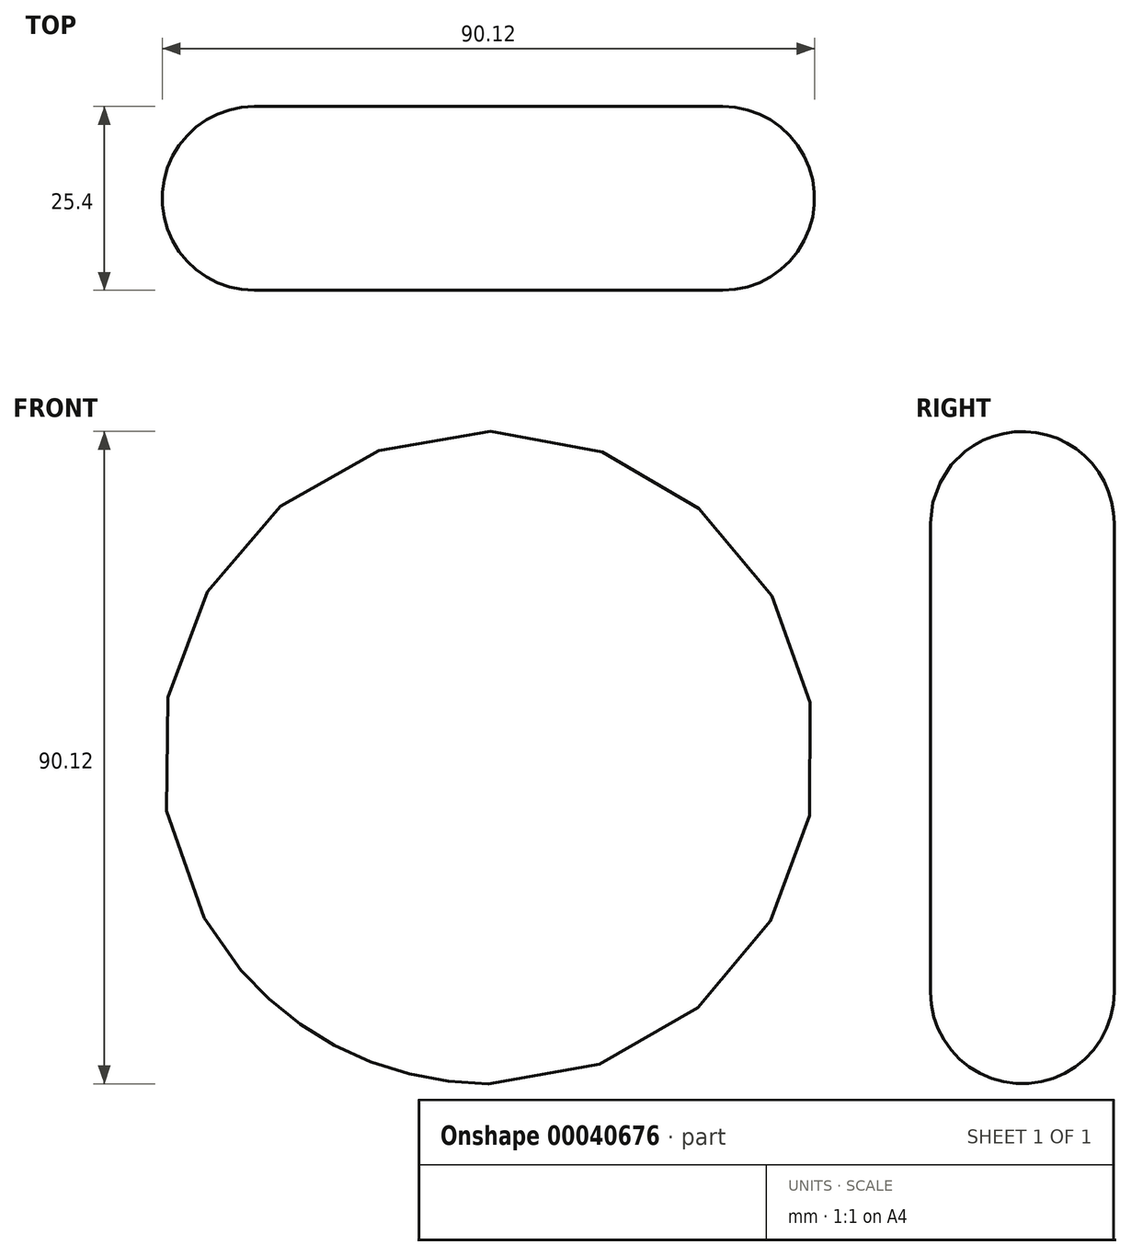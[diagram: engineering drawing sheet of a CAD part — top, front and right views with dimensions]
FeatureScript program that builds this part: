
annotation { "Feature Type Name" : "Feature", "Feature Type Description" : "" }
export const myFeature = defineFeature(function(context is Context, id is Id, definition is map)
    precondition{}
    {
        {
            var Q0;
            Q0=qCreatedBy(makeId("Front.planeOp"),FACE);
            var sketch = newSketch(context, id + "F0", { "sketchPlane" : qUnion([Q0])});
            skCircle(sketch, "E0", {"center": v(0, 0) * mm, "radius": 45.06 * mm});
            skSolve(sketch);
        }
        {
            var Q0;
            Q0 = qSketchRegion(id + "F0", true);
            var Q1;
            Q1=makeQuery(id+"F0.imprint","IMPRINT",FACE,{"disambiguationData":[TD([[makeQuery(id+"F0.imprint","IMPRINT",EDGE,{"derivedFrom":sQuery(id+"F0.wireOp",EDGE,"E0")}),1.0]])]});
            extrude(context, id + "F1", {"entities" : qUnion([Q0, Q1]), "depth" : 25.4 * mm});
        }
        {
            var Q0;
            Q0=makeQuery(id+"F1.opExtrude","CAP_EDGE",EDGE,{"disambiguationData":[OSD([sQuery(id+"F0.wireOp",EDGE,"E0")])],"isStart":false});
            var Q1;
            Q1=makeQuery(id+"F1.opExtrude","CAP_EDGE",EDGE,{"disambiguationData":[OSD([sQuery(id+"F0.wireOp",EDGE,"E0")])],"isStart":true});
            fillet(context, id + "F2", {"entities" : qUnion([Q0, Q1]), "radius" : 12.7 * mm, "tangentPropagation" : true, "allowEdgeOverflow" : false});
        }
    });
